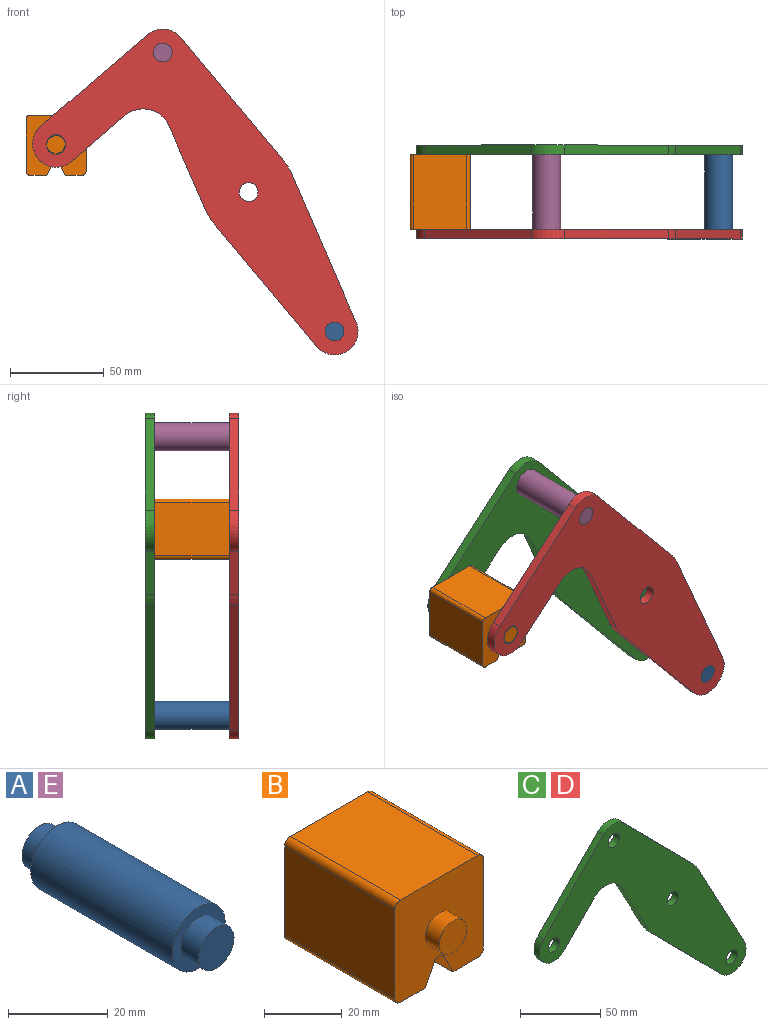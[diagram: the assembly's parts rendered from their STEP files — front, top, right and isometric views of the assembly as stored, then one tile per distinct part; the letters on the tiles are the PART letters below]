
ASSEMBLY  parts=5 mates=3
PART A: 7 faces, bbox 15x50x15 mm
  f0: cylinder r=7.5mm len=40mm, axis (0,-1,0), area 1885mm2, adj f2,f5
  f1: cylinder r=5mm len=10mm, axis (0,1,0), area 157.1mm2, adj f2,f3
  f2: plane 15x15mm, normal (0,-1,0), area 98.2mm2, adj f0,f1
  f3: plane 10x10mm, normal (0,-1,0), area 78.5mm2, adj f1
  f4: cylinder r=5mm len=10mm, axis (0,-1,0), area 157.1mm2, adj f5,f6
  f5: plane 15x15mm, normal (0,1,0), area 98.2mm2, adj f0,f4
  f6: plane 10x10mm, normal (0,1,0), area 78.5mm2, adj f4
PART B: 18 faces, bbox 32.1x50x32.1 mm
  f0: plane 40x28.08mm, normal (1,0,0), area 1123.1mm2, adj f4,f10,f13,f14
  f1: plane 40x9.04mm, normal (0,0,-1), area 361.6mm2, adj f2,f4,f10,f14
  f2: plane 40x6.42mm, normal (-0.89,0,-0.45), area 287.2mm2, adj f1,f4,f10,f15
  f3: plane 40x6.42mm, normal (0.89,0,-0.45), area 287.2mm2, adj f4,f5,f10,f15
  f4: plane 32.08x32.08mm, normal (0,-1,0), area 900.6mm2, adj f0,f1,f2,f3,f5,f6,f7,f9
  f5: plane 40x9.04mm, normal (0,0,-1), area 361.6mm2, adj f3,f4,f10,f16
  f6: plane 40x28.08mm, normal (0,0,1), area 1123.1mm2, adj f4,f10,f13,f17
  f7: plane 40x28.08mm, normal (-1,0,0), area 1123.1mm2, adj f4,f10,f16,f17
  f8: plane 10x10mm, normal (0,-1,0), area 78.5mm2, adj f9
  f9: cylinder r=5mm len=10mm, axis (0,1,0), area 157.1mm2, adj f4,f8
  f10: plane 32.08x32.08mm, normal (0,1,0), area 900.6mm2, adj f0,f1,f2,f3,f5,f6,f7,f12
  f11: plane 10x10mm, normal (0,1,0), area 78.5mm2, adj f12
  f12: cylinder r=5mm len=10mm, axis (0,-1,0), area 157.1mm2, adj f10,f11
  f13: cylinder r=2mm len=40mm, axis (0,1,0), area 125.7mm2, adj f0,f4,f6,f10
  f14: cylinder r=2mm len=40mm, axis (0,-1,0), area 125.7mm2, adj f0,f1,f4,f10
  f15: cylinder r=2mm len=40mm, axis (0,1,0), area 177.1mm2, adj f2,f3,f4,f10
  f16: cylinder r=2mm len=40mm, axis (0,1,0), area 125.7mm2, adj f4,f5,f7,f10
  f17: cylinder r=2mm len=40mm, axis (0,-1,0), area 125.7mm2, adj f4,f6,f7,f10
PART C: 18 faces, bbox 181.7x5x165.8 mm
  f0: plane 43.49x23.35mm, normal (-0.88,0,-0.47), area 246.8mm2, adj f1,f14,f16,f17
  f1: cylinder r=25mm len=5.75mm, axis (0,1,0), area 35.8mm2, adj f0,f2,f16,f17
  f2: plane 61.6x60.87mm, normal (-0.71,0,-0.7), area 433mm2, adj f1,f3,f16,f17
  f3: cylinder r=12.5mm len=21.39mm, axis (0,1,0), area 178.4mm2, adj f2,f4,f16,f17
  f4: plane 76.3x40.96mm, normal (0.88,0,0.47), area 433mm2, adj f3,f5,f16,f17
  f5: cylinder r=25mm len=5.75mm, axis (0,1,0), area 35.8mm2, adj f4,f6,f16,f17
  f6: plane 61.6x60.87mm, normal (0.71,0,0.7), area 433mm2, adj f5,f7,f16,f17
  f7: cylinder r=12.5mm len=17.78mm, axis (0,1,0), area 98.9mm2, adj f6,f8,f16,f17
  f8: plane 53.35x52.71mm, normal (-0.71,0,0.7), area 375mm2, adj f7,f9,f16,f17
  f9: cylinder r=12.5mm len=21.39mm, axis (0,1,0), area 196.3mm2, adj f8,f10,f16,f17
  f10: plane 26.86x26.54mm, normal (0.71,0,-0.7), area 188.8mm2, adj f9,f14,f16,f17
  f11: cylinder r=5mm len=10mm, axis (0,1,0), area 157.1mm2, adj f16,f17
  f12: cylinder r=5mm len=10mm, axis (0,1,0), area 157.1mm2, adj f16,f17
  f13: cylinder r=5mm len=10mm, axis (0,1,0), area 157.1mm2, adj f16,f17
  f14: cylinder r=15mm len=23.89mm, axis (0,1,0), area 140.2mm2, adj f0,f10,f16,f17
  f15: cylinder r=5mm len=10mm, axis (0,1,0), area 157.1mm2, adj f16,f17
  f16: plane 181.66x165.78mm, normal (0,-1,0), area 8710.1mm2, adj f0,f1,f2,f3,f4,f5,f6,f7
  f17: plane 181.66x165.78mm, normal (0,1,0), area 8710.1mm2, adj f0,f1,f2,f3,f4,f5,f6,f7
PART D: same geometry as C
PART E: same geometry as A
PLACE A rot(axis=(0,1,0),4.8deg) t=(86.83,-18.83,-154.5)mm
PLACE B t=(-3.21,-18.83,2.49)mm
PLACE C rot(axis=(0,1,0),4.8deg) t=(-5,26.17,-5.53)mm
PLACE D rot(axis=(0,1,0),4.8deg) t=(-5,-18.83,-5.53)mm fixed
PLACE E rot(axis=(0,1,0),4.8deg) t=(-5,-18.83,-5.53)mm
MATE revolute D.f9 <-> B.f4  axis (0,1,0) through (-107.9,-18.83,20.2)mm
MATE fastened E.f0 <-> C.f7  axis (0,1,0) through (-50.91,21.17,68.96)mm
MATE fastened A.f0 <-> D.f3  axis (0,-1,0) through (40.91,-18.83,-80.01)mm
